# Revit family: РИДАН_Датчик температуры MBT3281
name_source: partatom
category: Арматура трубопроводов
units: mm (PartAtom-declared; Revit-internal decimal feet)

## family parameters
Всегда вертикально = Да
На основе рабочей плоскости = Нет
Общий = Нет
При загрузке вырезать с полостями = Нет
Размер круглого соединителя = Использовать диаметр
Тип детали = Нормальный

## types (4) — shared parameters
ADSK_Версия Revit = 2019
ADSK_Версия семейства = 1.0
ADSK_Единица измерения = шт.
ADSK_Завод-изготовитель = ООО «Ридан-Трейд»
ADSK_Количество = 1
ADSK_Марка = MBT3281

## per-type parameters (varying)
| type | ADSK_Код изделия | ADSK_Масса | ADSK_Наименование |
| MBT3281 уличный Pt1000 | 097U0115 | 0.058 | Термопреобразователь сопротивления наружнего воздуха MBT 3281, чувствительный элемент Pt1000 |
| MBT3281 уличный NTC10k | 097U0116 | 0.058 | Термопреобразователь сопротивления наружнего воздуха MBT 3281, чувствительный элемент NTC10K |
| MBT3281 накладной Pt1000 | 097U0113 | 0.105 | Термопреобразователь сопротивления накладной MBT 3281, чувствительный элемент Pt1000 |
| MBT3281 накладной  NTC10k | 097U0114 | 0.105 | Термопреобразователь сопротивления накладной MBT 3281, чувствительный элемент NTC10K |
